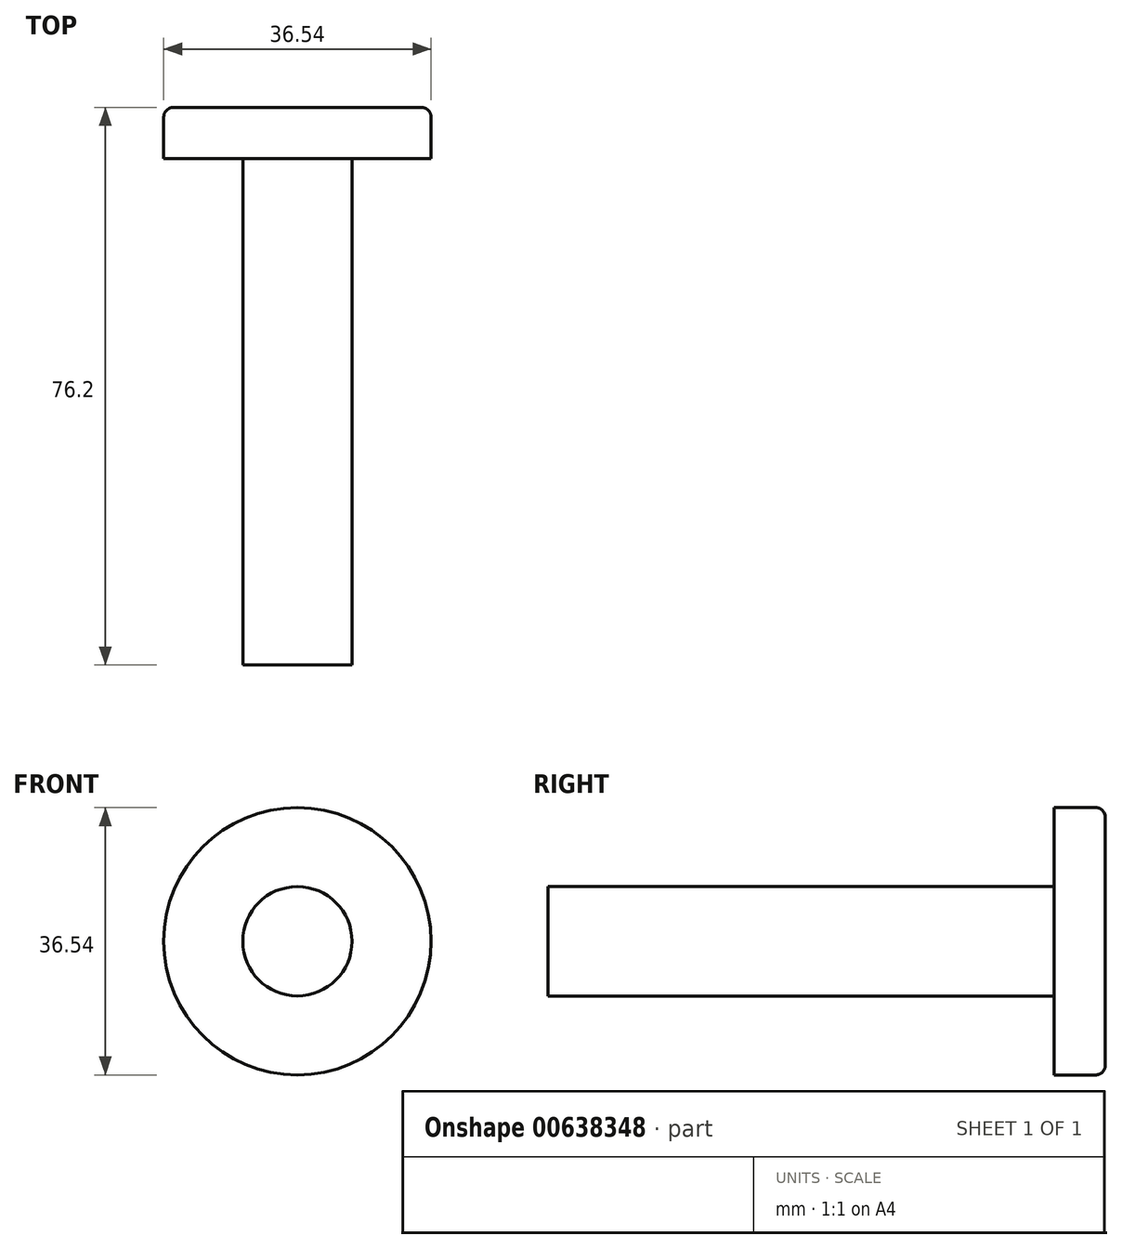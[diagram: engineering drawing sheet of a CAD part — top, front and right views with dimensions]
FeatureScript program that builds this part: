
annotation { "Feature Type Name" : "Feature", "Feature Type Description" : "" }
export const myFeature = defineFeature(function(context is Context, id is Id, definition is map)
    precondition{}
    {
        {
            var Q0;
            Q0=qCreatedBy(makeId("Front.planeOp"),FACE);
            var sketch = newSketch(context, id + "F0", { "sketchPlane" : qUnion([Q0])});
            skCircle(sketch, "E0", {"center": v(0, 0) * mm, "radius": 7.47 * mm});
            skSolve(sketch);
        }
        {
            var Q0;
            Q0=makeQuery(id+"F0.imprint","IMPRINT",FACE,{"disambiguationData":[TD([[makeQuery(id+"F0.imprint","IMPRINT",EDGE,{"derivedFrom":sQuery(id+"F0.wireOp",EDGE,"E0")}),1.0]])]});
            extrude(context, id + "F1", {"entities" : qUnion([Q0]), "depth" : 76.2 * mm, "offsetDistance" : 25.4 * mm});
        }
        {
            var Q0;
            Q0=qCreatedBy(makeId("Front.planeOp"),FACE);
            var sketch = newSketch(context, id + "F2", { "sketchPlane" : qUnion([Q0])});
            skCircle(sketch, "E1", {"center": v(0, 0) * mm, "radius": 18.27 * mm});
            skSolve(sketch);
        }
        {
            var Q0;
            Q0=makeQuery(id+"F2.imprint","IMPRINT",FACE,{"disambiguationData":[TD([[makeQuery(id+"F2.imprint","IMPRINT",EDGE,{"derivedFrom":sQuery(id+"F2.wireOp",EDGE,"E1")}),1.0]])]});
            extrude(context, id + "F3", {"entities" : qUnion([Q0]), "operationType" : NewBodyOperationType.ADD, "depth" : 7 * mm, "offsetDistance" : 25.4 * mm});
        }
        {
            var Q0;
            Q0=makeQuery(id+"F3.opExtrude","CAP_EDGE",EDGE,{"disambiguationData":[OSD([sQuery(id+"F2.wireOp",EDGE,"E1")])],"isStart":true});
            fillet(context, id + "F4", {"entities" : qUnion([Q0]), "radius" : 1.27 * mm, "tangentPropagation" : true, "allowEdgeOverflow" : false});
        }
    });
